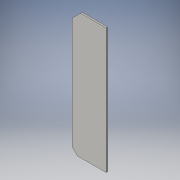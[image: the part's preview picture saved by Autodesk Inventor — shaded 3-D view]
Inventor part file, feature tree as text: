
AUTODESK INVENTOR PART (.ipt)
format: ipt  version: 2016 (Build 200138000, 138)  size: 97,792 bytes
history: native  units: in
note: dims shown in document units (in); Inventor stores cm internally (conversion verified against a paired STEP export)
features: chamfer x2, extrude x1, fillet x1, sketch x1
ambient origin geometry x8: Origin, YZ Plane, XZ Plane, XY Plane, X Axis, Y Axis, Z Axis, Center Point
bodies: Solid1 (feature_tree)
feature tree (5):
  extrude  "Extrusion1"  Depth=12.0in
  chamfer  "Chamfer1"  Distance=0.15in
  chamfer  "Chamfer2"  Distance=0.125in Angle=45.0deg
  fillet  "Fillet1"  Radius=0.125in
  sketch  "Sketch1"  dims[d0=3.25in d1=12.0in d2=0.15in d3=0.0in d4=0.5in d5=0.125in d6=45.0deg d7=0.8in d8=0.125in d9=45.0deg d10=0.125in]
